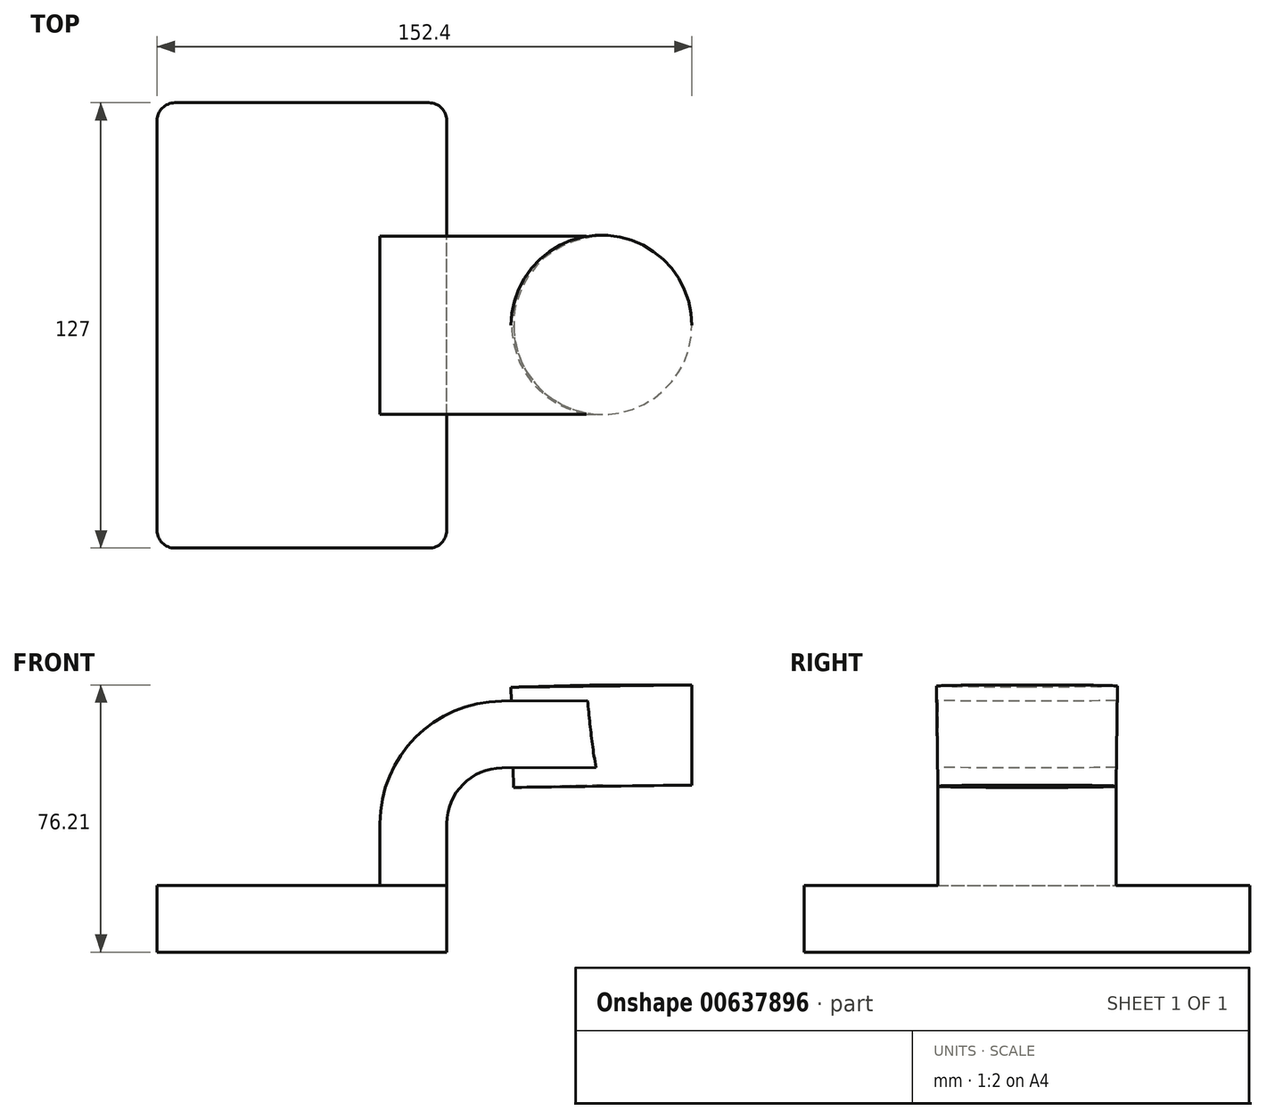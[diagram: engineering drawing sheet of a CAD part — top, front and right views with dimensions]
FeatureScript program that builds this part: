
annotation { "Feature Type Name" : "Feature", "Feature Type Description" : "" }
export const myFeature = defineFeature(function(context is Context, id is Id, definition is map)
    precondition{}
    {
        {
            var Q0;
            Q0=qCreatedBy(makeId("Front.planeOp"),FACE);
            var sketch = newSketch(context, id + "F0", { "sketchPlane" : qUnion([Q0])});
            skLineSegment(sketch, "E0.bottom", {"start": v(-41.27, 9.53) * mm, "end": v(41.28, 9.53) * mm});
            skLineSegment(sketch, "E0.top", {"start": v(-41.28, -9.52) * mm, "end": v(41.27, -9.52) * mm});
            skLineSegment(sketch, "E0.left", {"start": v(-41.28, 9.53) * mm, "end": v(-41.28, -9.52) * mm});
            skLineSegment(sketch, "E0.right", {"start": v(41.28, 9.53) * mm, "end": v(41.27, -9.52) * mm});
            skPoint(sketch, "E0.middle", {"position": v(0, 0) * mm});
            skLineSegment(sketch, "E1.bottom", {"start": v(111.12, 66.68) * mm, "end": v(60.32, 66.68) * mm});
            skLineSegment(sketch, "E1.top", {"start": v(111.12, 38.1) * mm, "end": v(60.32, 38.1) * mm});
            skLineSegment(sketch, "E1.left", {"start": v(111.12, 66.68) * mm, "end": v(111.12, 38.1) * mm});
            skLineSegment(sketch, "E1.right", {"start": v(60.32, 66.68) * mm, "end": v(60.32, 38.1) * mm});
            skPoint(sketch, "E1.middle", {"position": v(85.72, 52.39) * mm});
            skLineSegment(sketch, "E2", {"start": v(41.28, 9.52) * mm, "end": v(41.28, 27.1) * mm});
            skArc(sketch, "E3", {"start": v(41.28, 27.1) * mm, "mid": v(45.89, 38.3) * mm, "end": v(57.04, 42.98) * mm});
            skLineSegment(sketch, "E4", {"start": v(57.04, 42.98) * mm, "end": v(85.48, 43.18) * mm});
            skLineSegment(sketch, "E5.0", {"start": v(56.91, 62.03) * mm, "end": v(85.35, 62.23) * mm});
            skArc(sketch, "E5.1", {"start": v(22.23, 27.1) * mm, "mid": v(32.37, 51.72) * mm, "end": v(56.91, 62.03) * mm});
            skLineSegment(sketch, "E5.2", {"start": v(22.23, 9.52) * mm, "end": v(22.23, 27.1) * mm});
            skLineSegment(sketch, "E6", {"start": v(85.72, 38.1) * mm, "end": v(85.35, 66.68) * mm});
            skLineSegment(sketch, "E7", {"start": v(85.35, 66.68) * mm, "end": v(85.48, 43.18) * mm});
            skLineSegment(sketch, "E8", {"start": v(85.72, 52.39) * mm, "end": v(85.35, 62.23) * mm});
            skFitSpline(sketch, "E9", {"points": [v(-41.28, 9.52) * mm, v(56.91, 62.03) * mm], "startDerivative": vector(0.4, 95.74) * mm, "endDerivative": vector(140.3, -0.8) * mm});
            skLineSegment(sketch, "E10", {"start": v(85.35, 66.68) * mm, "end": v(85.72, 38.1) * mm});
            skSolve(sketch);
        }
        {
            var Q0;
            Q0=makeQuery(id+"F0.imprint","IMPRINT",FACE,{"disambiguationData":[TD([[makeQuery(id+"F0.imprint","IMPRINT",EDGE,{"derivedFrom":sQuery(id+"F0.wireOp",EDGE,"E0.top")}),1.0]])]});
            extrude(context, id + "F1", {"entities" : qUnion([Q0]), "endBound" : BoundingType.SYMMETRIC, "depth" : 127 * mm, "offsetDistance" : 25.4 * mm});
        }
        {
            var Q0;
            {var subQ1=sQuery(id+"F0.wireOp",EDGE,"E2");Q0=makeQuery(id+"F0.imprint","IMPRINT",FACE,{"disambiguationData":[TD([[makeQuery(id+"F0.imprint","IMPRINT",EDGE,{"derivedFrom":subQ1}),1.0]])]});}
            var Q1;
            {var subQ5=sQuery(id+"F0.wireOp",EDGE,"E5.0");var subQ7=sQuery(id+"F0.wireOp",EDGE,"E1.right");var subQ8=makeQuery(id+"F0.imprint","INTERSECT",VERTEX,{"derivedFrom":[subQ7,subQ5]});Q1=makeQuery(id+"F0.imprint","IMPRINT",FACE,{"disambiguationData":[TD([[makeQuery(id+"F0.imprint","IMPRINT",EDGE,{"disambiguationData":[TD([[subQ8,-1.0]])],"derivedFrom":subQ7}),1.0]])]});}
            extrude(context, id + "F2", {"entities" : qUnion([Q0, Q1]), "operationType" : NewBodyOperationType.ADD, "endBound" : BoundingType.SYMMETRIC, "depth" : 50.8 * mm, "offsetDistance" : 25.4 * mm});
        }
        {
            var Q0;
            Q0=makeQuery(id+"F0.imprint","IMPRINT",FACE,{"disambiguationData":[TD([[makeQuery(id+"F0.imprint","IMPRINT",EDGE,{"derivedFrom":sQuery(id+"F0.wireOp",EDGE,"E5.1")}),1.0]])]});
            extrude(context, id + "F3", {"entities" : qUnion([Q0]), "operationType" : NewBodyOperationType.ADD, "endBound" : BoundingType.SYMMETRIC, "depth" : 15.88 * mm, "offsetDistance" : 25.4 * mm});
        }
        {
            var Q0;
            {var subQ4=sQuery(id+"F0.wireOp",EDGE,"E1.left");Q0=makeQuery(id+"F0.imprint","IMPRINT",FACE,{"disambiguationData":[TD([[makeQuery(id+"F0.imprint","IMPRINT",EDGE,{"derivedFrom":subQ4}),-1.0]])]});}
            var Q1;
            Q1=sQuery(id+"F0.wireOp",EDGE,"E10");
            revolve(context, id + "F4", {"operationType" : NewBodyOperationType.ADD, "entities" : qUnion([Q0]), "axis" : qUnion([Q1]), "revolveType" : RevolveType.FULL});
        }
        {
            var Q0;
            Q0=makeQuery(id+"F1.opExtrude","CAP_EDGE",EDGE,{"disambiguationData":[OSD([sQuery(id+"F0.wireOp",EDGE,"E0.right")])],"isStart":false});
            var Q1;
            Q1=makeQuery(id+"F1.opExtrude","CAP_EDGE",EDGE,{"disambiguationData":[OSD([sQuery(id+"F0.wireOp",EDGE,"E0.left")])],"isStart":false});
            var Q2;
            Q2=makeQuery(id+"F1.opExtrude","CAP_EDGE",EDGE,{"disambiguationData":[OSD([sQuery(id+"F0.wireOp",EDGE,"E0.left")])],"isStart":true});
            var Q3;
            Q3=makeQuery(id+"F1.opExtrude","CAP_EDGE",EDGE,{"disambiguationData":[OSD([sQuery(id+"F0.wireOp",EDGE,"E0.right")])],"isStart":true});
            fillet(context, id + "F5", {"entities" : qUnion([Q0, Q1, Q2, Q3]), "radius" : 5.08 * mm, "tangentPropagation" : true, "allowEdgeOverflow" : false});
        }
    });
